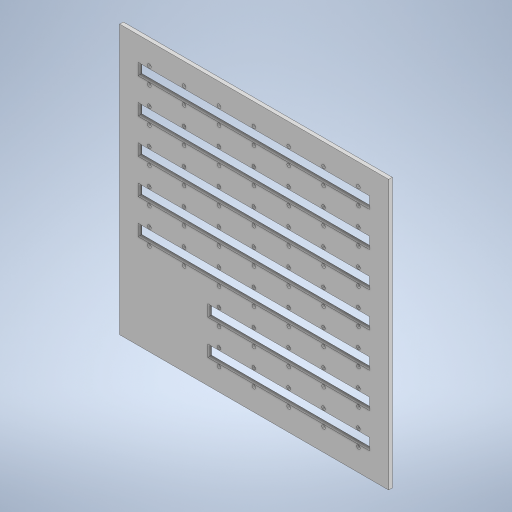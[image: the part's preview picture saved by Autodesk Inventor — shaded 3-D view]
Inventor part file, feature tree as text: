
AUTODESK INVENTOR PART (.ipt)
format: ipt  version: 2023 (Build 270158000, 158)  size: 397,824 bytes
history: native  units: mm
features: extrude x8, sketch x8, pattern_linear x6
ambient origin geometry x8: Origin, YZ Plane, XZ Plane, XY Plane, X Axis, Y Axis, Z Axis, Center Point
bodies: Solid1 (feature_tree)
feature tree (22):
  extrude  "Extrusion1"  Depth=220.0mm
  extrude  "Extrusion5"  Depth=3.0mm TaperAngle=0.0deg
  pattern_linear  "Rectangular Pattern3"  Count1=7 Spacing1=28.5mm
  extrude  "Extrusion6"  Depth=3.0mm TaperAngle=0.0deg
  pattern_linear  "Rectangular Pattern4"  Count1=5 Spacing1=28.5mm
  extrude  "Extrusion7"  Depth=28.5mm
  pattern_linear  "Rectangular Pattern5"  Count1=7 Spacing1=28.5mm
  extrude  "Extrusion8"  Depth=28.5mm
  pattern_linear  "Rectangular Pattern6"  Spacing1=6.75mm  [1 undecoded]
  extrude  "Extrusion9"  Depth=28.5mm
  extrude  "Extrusion10"  Depth=3.0mm
  pattern_linear  "Rectangular Pattern7"  Spacing1=3.0mm  [1 undecoded]
  extrude  "Extrusion11"  Depth=3.0mm TaperAngle=0.0deg
  pattern_linear  "Rectangular Pattern9"  Count1=5 Spacing1=28.5mm
  sketch  "Sketch1"  dims[d0=220.0mm d1=220.0mm]
  sketch  "Sketch5"  dims[d2=3.0mm d3=0.0mm d36=3.0mm d37=0.0mm d38=70.0mm d40=28.5mm]
  sketch  "Sketch6"  dims[d41=50.0mm d43=28.5mm d44=3.0mm d45=0.0mm d46=50.0mm d48=28.5mm]
  sketch  "Sketch7"  dims[d49=20.0mm d51=28.5mm d52=6.75mm]
  sketch  "Sketch8"  dims[d53=13.5mm]
  sketch  "Sketch9"  dims[d54=3.0mm]
  sketch  "Sketch10"  dims[d55=3.0mm]
  sketch  "Sketch11"  dims[d56=10.0mm d57=0.0mm d58=70.0mm d60=28.5mm d61=50.0mm d63=28.5mm d64=6.75mm d65=13.5mm d66=3.0mm d67=3.0mm d68=3.0mm d69=0.0mm d70=50.0mm d72=28.5mm d73=20.0mm d75=28.5mm d76=9.5mm d77=3.0mm d78=0.0mm d79=6.0mm d80=0.0mm d81=50.0mm d83=28.5mm d84=9.5mm d85=6.0mm d86=0.0mm d90=20.0mm d92=28.5mm d39=0.872665mm d93=0.5mm d94=0.872665mm d95=0.5mm d96=0.872665mm]
note: 2 required parameter values undecoded (feature->parameter linkage not recoverable at this tier; creation-order binding heuristic only, values carry confidence <= 0.55)
